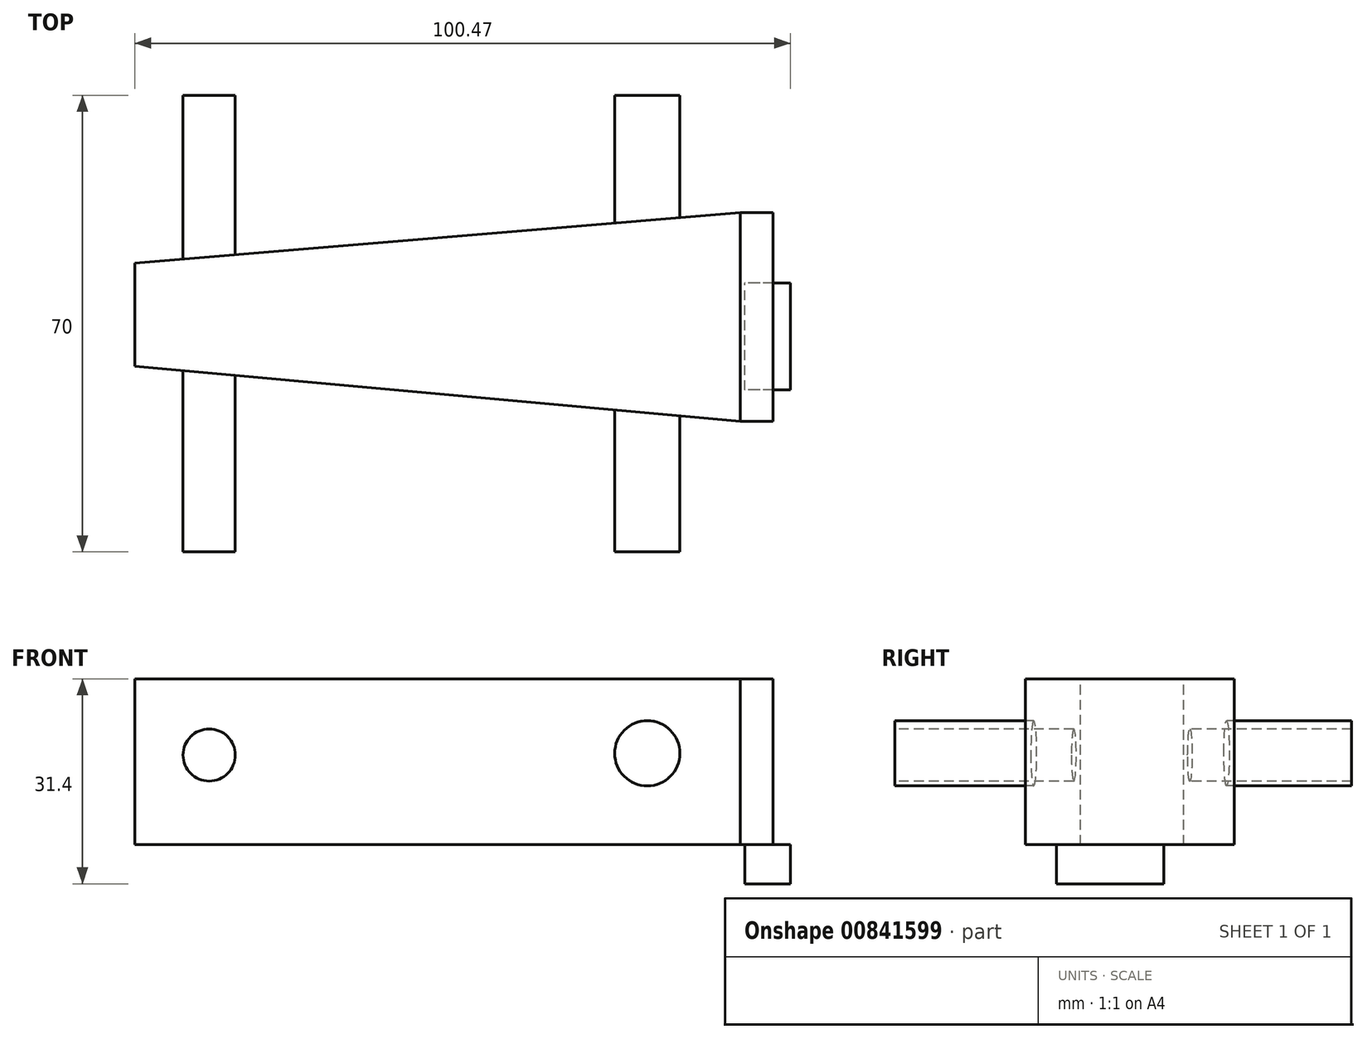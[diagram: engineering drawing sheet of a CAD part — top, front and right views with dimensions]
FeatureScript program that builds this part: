
annotation { "Feature Type Name" : "Feature", "Feature Type Description" : "" }
export const myFeature = defineFeature(function(context is Context, id is Id, definition is map)
    precondition{}
    {
        {
            var Q0;
            Q0=qCreatedBy(makeId("Top.planeOp"),FACE);
            var sketch = newSketch(context, id + "F0", { "sketchPlane" : qUnion([Q0])});
            skLineSegment(sketch, "E0.bottom", {"start": v(-20.3, 32.04) * mm, "end": v(72.48, 32.04) * mm});
            skLineSegment(sketch, "E0.top", {"start": v(-20.3, 0) * mm, "end": v(72.48, 0) * mm});
            skLineSegment(sketch, "E0.left", {"start": v(-20.3, 32.04) * mm, "end": v(-20.3, 0) * mm});
            skLineSegment(sketch, "E0.right", {"start": v(72.48, 32.04) * mm, "end": v(72.48, 0) * mm});
            skSolve(sketch);
        }
        {
            var Q0;
            Q0=makeQuery(id+"F0.imprint","IMPRINT",FACE,{"disambiguationData":[TD([[makeQuery(id+"F0.imprint","IMPRINT",EDGE,{"derivedFrom":sQuery(id+"F0.wireOp",EDGE,"E0.bottom")}),-1.0]])]});
            extrude(context, id + "F1", {"entities" : qUnion([Q0]), "depth" : 25.4 * mm, "offsetDistance" : 25.4 * mm});
        }
        {
            var Q0;
            Q0=makeQuery(id+"F1.opExtrude","CAP_FACE",FACE,{"disambiguationData":[OSD([sQuery(id+"F0.wireOp",EDGE,"E0.bottom"),sQuery(id+"F0.wireOp",EDGE,"E0.top"),sQuery(id+"F0.wireOp",EDGE,"E0.left"),sQuery(id+"F0.wireOp",EDGE,"E0.right")])],"isStart":false});
            var sketch = newSketch(context, id + "F2", { "sketchPlane" : qUnion([Q0])});
            skLineSegment(sketch, "E1", {"start": v(72.48, 32.04) * mm, "end": v(-20.3, 24.25) * mm});
            skLineSegment(sketch, "E2", {"start": v(72.48, 0) * mm, "end": v(-20.3, 8.47) * mm});
            skSolve(sketch);
        }
        {
            var Q0;
            {var subQ0=sQuery(id+"F2.wireOp",EDGE,"E1");Q0=makeQuery(id+"F2.imprint","IMPRINT",FACE,{"disambiguationData":[TD([[makeQuery(id+"F2.imprint","IMPRINT",EDGE,{"derivedFrom":subQ0}),-1.0]])]});}
            var Q1;
            {var subQ0=sQuery(id+"F2.wireOp",EDGE,"E2");Q1=makeQuery(id+"F2.imprint","IMPRINT",FACE,{"disambiguationData":[TD([[makeQuery(id+"F2.imprint","IMPRINT",EDGE,{"derivedFrom":subQ0}),1.0]])]});}
            extrude(context, id + "F3", {"entities" : qUnion([Q0, Q1]), "operationType" : NewBodyOperationType.REMOVE, "oppositeDirection" : true, "depth" : 25 * mm, "offsetDistance" : 25 * mm});
        }
        {
            var Q0;
            Q0=makeQuery(id+"F3.boolean.opBoolean","COPY",FACE,{"derivedFrom":makeQuery(id+"F3.opExtrude","CAP_FACE",FACE,{"disambiguationData":[OSD([sQuery(id+"F0.wireOp",EDGE,"E0.bottom"),sQuery(id+"F0.wireOp",EDGE,"E0.left"),sQuery(id+"F2.wireOp",EDGE,"E1")])],"isStart":false})});
            var Q1;
            Q1=makeQuery(id+"F3.boolean.opBoolean","COPY",FACE,{"derivedFrom":makeQuery(id+"F3.opExtrude","CAP_FACE",FACE,{"disambiguationData":[OSD([sQuery(id+"F0.wireOp",EDGE,"E0.top"),sQuery(id+"F0.wireOp",EDGE,"E0.left"),sQuery(id+"F2.wireOp",EDGE,"E2")])],"isStart":false})});
            extrude(context, id + "F4", {"entities" : qUnion([Q0, Q1]), "operationType" : NewBodyOperationType.REMOVE, "oppositeDirection" : true, "depth" : 25 * mm, "offsetDistance" : 25 * mm});
        }
        {
            var Q0;
            Q0=qCreatedBy(makeId("Top.planeOp"),FACE);
            var sketch = newSketch(context, id + "F5", { "sketchPlane" : qUnion([Q0])});
            skLineSegment(sketch, "E3", {"start": v(73.17, 4.8) * mm, "end": v(-19.5, 12.71) * mm});
            skLineSegment(sketch, "E4.bottom", {"start": v(73.17, 4.8) * mm, "end": v(60.17, 4.8) * mm});
            skLineSegment(sketch, "E4.top", {"start": v(73.17, 21.19) * mm, "end": v(60.17, 21.19) * mm});
            skLineSegment(sketch, "E4.left", {"start": v(73.17, 4.8) * mm, "end": v(73.17, 21.19) * mm});
            skLineSegment(sketch, "E4.right", {"start": v(60.17, 4.8) * mm, "end": v(60.17, 21.19) * mm});
            skLineSegment(sketch, "E5", {"start": v(60.17, 21.19) * mm, "end": v(-19.5, 21.19) * mm});
            skSolve(sketch);
        }
        {
            var Q0;
            Q0=sQuery(id+"F5.wireOp",EDGE,"E5");
            var Q1;
            Q1=sQuery(id+"F5.wireOp",EDGE,"E4.top");
            var Q2;
            Q2=sQuery(id+"F5.wireOp",EDGE,"E4.left");
            var Q3;
            Q3=sQuery(id+"F5.wireOp",EDGE,"E3");
            extrude(context, id + "F6", {"bodyType" : ToolBodyType.SURFACE, "surfaceEntities" : qUnion([Q0, Q1, Q2, Q3]), "oppositeDirection" : true, "depth" : 6 * mm, "offsetDistance" : 25 * mm});
        }
        {
            var Q0;
            Q0=makeQuery(id+"F6.opExtrude","SWEPT_FACE",FACE,{"disambiguationData":[OSD([sQuery(id+"F5.wireOp",EDGE,"E4.left")])]});
            extrude(context, id + "F7", {"entities" : qUnion([Q0]), "operationType" : NewBodyOperationType.ADD, "oppositeDirection" : true, "depth" : 7 * mm, "offsetDistance" : 25 * mm});
        }
        {
            var Q0;
            Q0=makeQuery(id+"F1.opExtrude","SWEPT_FACE",FACE,{"disambiguationData":[OSD([sQuery(id+"F0.wireOp",EDGE,"E0.right")])]});
            extrude(context, id + "F8", {"entities" : qUnion([Q0]), "depth" : 5 * mm, "offsetDistance" : 25 * mm});
        }
        {
            var Q0;
            Q0=qCreatedBy(makeId("Front.planeOp"),FACE);
            var sketch = newSketch(context, id + "F9", { "sketchPlane" : qUnion([Q0])});
            skCircle(sketch, "E6", {"center": v(58.25, 14) * mm, "radius": 5 * mm});
            skCircle(sketch, "E7", {"center": v(-8.89, 13.74) * mm, "radius": 4 * mm});
            skSolve(sketch);
        }
        {
            var Q0;
            Q0=makeQuery(id+"F9.imprint","IMPRINT",FACE,{"disambiguationData":[TD([[makeQuery(id+"F9.imprint","IMPRINT",EDGE,{"derivedFrom":sQuery(id+"F9.wireOp",EDGE,"E6")}),1.0]])]});
            var Q1;
            Q1=makeQuery(id+"F9.imprint","IMPRINT",FACE,{"disambiguationData":[TD([[makeQuery(id+"F9.imprint","IMPRINT",EDGE,{"derivedFrom":sQuery(id+"F9.wireOp",EDGE,"E7")}),1.0]])]});
            extrude(context, id + "F10", {"entities" : qUnion([Q0, Q1]), "operationType" : NewBodyOperationType.ADD, "oppositeDirection" : true, "depth" : 50 * mm, "offsetDistance" : 25 * mm, "hasSecondDirection" : true, "secondDirectionOppositeDirection" : false, "secondDirectionDepth" : 20 * mm});
        }
    });
